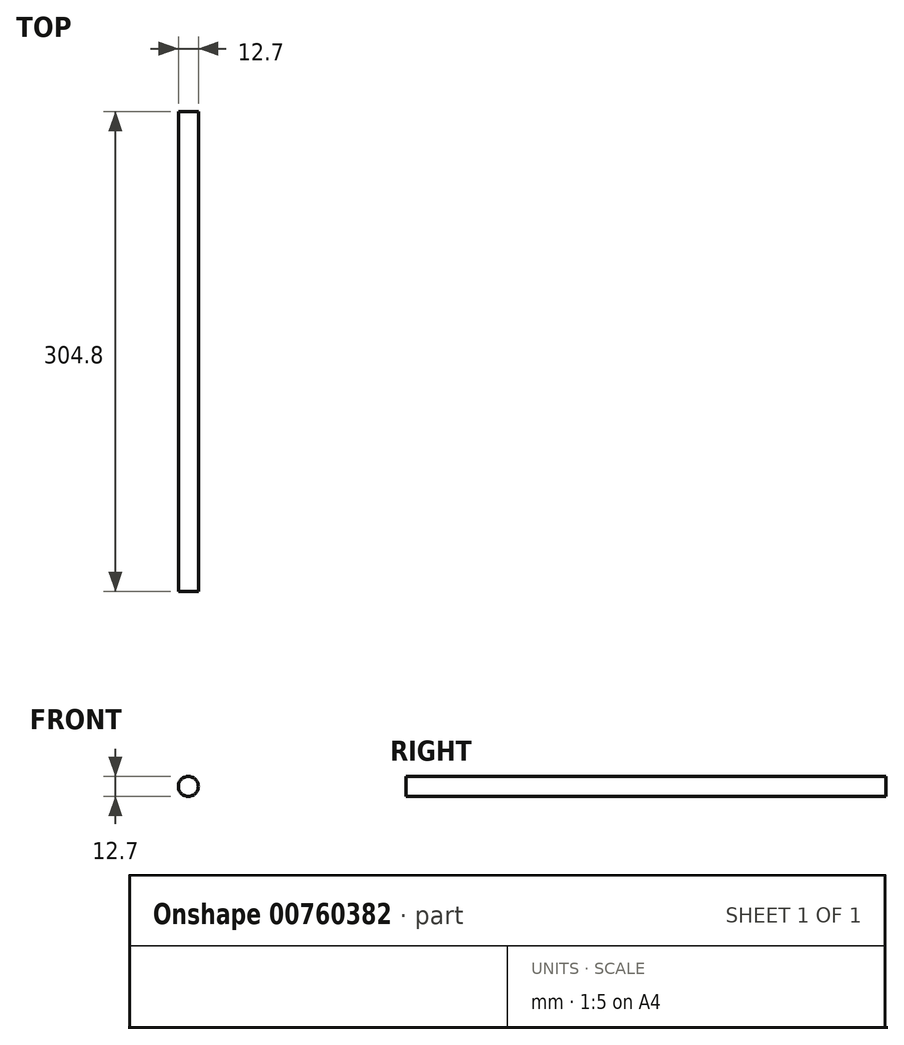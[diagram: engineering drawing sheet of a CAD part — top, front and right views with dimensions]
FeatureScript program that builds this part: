
annotation { "Feature Type Name" : "Feature", "Feature Type Description" : "" }
export const myFeature = defineFeature(function(context is Context, id is Id, definition is map)
    precondition{}
    {
        {
            var Q0;
            Q0=qCreatedBy(makeId("Front.planeOp"),FACE);
            var sketch = newSketch(context, id + "F0", { "sketchPlane" : qUnion([Q0])});
            skCircle(sketch, "E0", {"center": v(-21.5, -7.2) * mm, "radius": 6.35 * mm});
            skSolve(sketch);
        }
        {
            var Q0;
            Q0 = qSketchRegion(id + "F0", true);
            var sketch = newSketch(context, id + "F1", { "sketchPlane" : qUnion([Q0])});
            skSolve(sketch);
        }
        {
            var Q0;
            Q0=makeQuery(id+"F1.imprint","IMPRINT",FACE,{"disambiguationData":[TD([[makeQuery(id+"F1.imprint","IMPRINT",EDGE,{"derivedFrom":makeQuery(id+"F0.imprint","IMPRINT",EDGE,{"derivedFrom":sQuery(id+"F0.wireOp",EDGE,"E0")})}),1.0]])]});
            var Q1;
            Q1=sQuery(id+"F0.wireOp",EDGE,"E0");
            extrude(context, id + "F2", {"entities" : qUnion([Q0]), "bodyType" : ToolBodyType.SURFACE, "surfaceEntities" : qUnion([Q1]), "depth" : 304.8 * mm, "offsetDistance" : 25.4 * mm});
        }
    });
